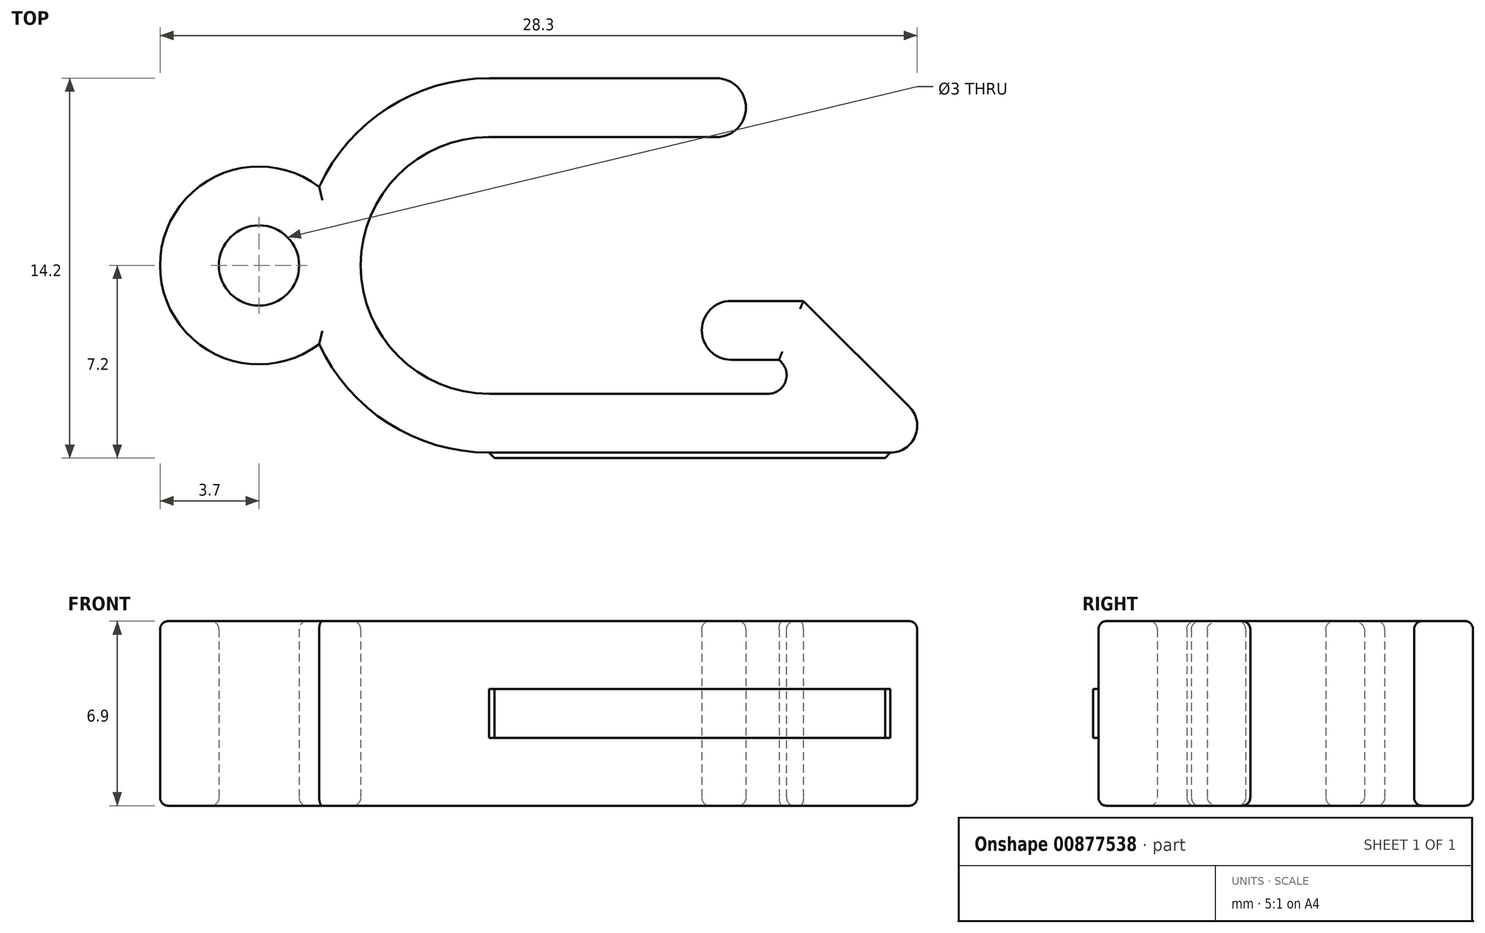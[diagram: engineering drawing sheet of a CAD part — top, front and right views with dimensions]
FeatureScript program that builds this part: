
annotation { "Feature Type Name" : "Feature", "Feature Type Description" : "" }
export const myFeature = defineFeature(function(context is Context, id is Id, definition is map)
    precondition{}
    {
        {
            var Q0;
            Q0=qCreatedBy(makeId("Top.planeOp"),FACE);
            var sketch = newSketch(context, id + "F0", { "sketchPlane" : qUnion([Q0])});
            skArc(sketch, "E0", {"start": v(0, 7) * mm, "mid": v(-7, 0) * mm, "end": v(0, -7) * mm});
            skLineSegment(sketch, "E1", {"start": v(0, 7) * mm, "end": v(8.5, 7) * mm});
            skArc(sketch, "E2", {"start": v(8.5, 7) * mm, "mid": v(9.6, 5.9) * mm, "end": v(8.5, 4.8) * mm});
            skLineSegment(sketch, "E3", {"start": v(8.5, 4.8) * mm, "end": v(0, 4.8) * mm});
            skArc(sketch, "E4", {"start": v(0, 4.8) * mm, "mid": v(-4.8, 0) * mm, "end": v(0, -4.8) * mm});
            skLineSegment(sketch, "E5", {"start": v(0, -4.8) * mm, "end": v(12.11, -4.8) * mm});
            skLineSegment(sketch, "E6", {"start": v(12.11, -4.8) * mm, "end": v(10.84, -3.53) * mm});
            skLineSegment(sketch, "E7", {"start": v(10.84, -3.53) * mm, "end": v(9.05, -3.53) * mm});
            skArc(sketch, "E8", {"start": v(9.05, -3.53) * mm, "mid": v(7.95, -2.43) * mm, "end": v(9.05, -1.33) * mm});
            skLineSegment(sketch, "E9", {"start": v(9.05, -1.33) * mm, "end": v(11.75, -1.33) * mm});
            skLineSegment(sketch, "E10", {"start": v(11.75, -1.33) * mm, "end": v(15.7, -5.29) * mm});
            skLineSegment(sketch, "E11", {"start": v(0, -7) * mm, "end": v(15, -7) * mm});
            skArc(sketch, "E12", {"start": v(15, -7) * mm, "mid": v(15.93, -6.38) * mm, "end": v(15.7, -5.29) * mm});
            skCircle(sketch, "E13", {"center": v(-8.6, 0) * mm, "radius": 1.5 * mm});
            skPoint(sketch, "E13.centerSnap0", {"position": v(-7, 0) * mm});
            skCircle(sketch, "E14", {"center": v(-8.6, 0) * mm, "radius": 3.7 * mm});
            skSolve(sketch);
        }
        {
            var Q0;
            Q0=makeQuery(id+"F0.imprint","IMPRINT",FACE,{"disambiguationData":[TD([[makeQuery(id+"F0.imprint","IMPRINT",EDGE,{"derivedFrom":sQuery(id+"F0.wireOp",EDGE,"E13")}),-1.0]])]});
            var Q1;
            {var subQ0=sQuery(id+"F0.wireOp",EDGE,"E14");var subQ1=sQuery(id+"F0.wireOp",EDGE,"E0");var subQ2=makeQuery(id+"F0.imprint","INTERSECT",VERTEX,{"disambiguationData":[OD(0.0)],"derivedFrom":[subQ1,subQ0]});Q1=makeQuery(id+"F0.imprint","IMPRINT",FACE,{"disambiguationData":[TD([[makeQuery(id+"F0.imprint","IMPRINT",EDGE,{"disambiguationData":[TD([[subQ2,-1.0]])],"derivedFrom":subQ1}),1.0]])]});}
            var Q2;
            {var subQ0=sQuery(id+"F0.wireOp",EDGE,"E1");Q2=makeQuery(id+"F0.imprint","IMPRINT",FACE,{"disambiguationData":[TD([[makeQuery(id+"F0.imprint","IMPRINT",EDGE,{"derivedFrom":subQ0}),-1.0]])]});}
            extrude(context, id + "F1", {"entities" : qUnion([Q0, Q1, Q2]), "depth" : 6.9 * mm, "offsetDistance" : 25 * mm});
        }
        {
            var Q0;
            Q0=makeQuery(id+"F1.opExtrude","SWEPT_EDGE",EDGE,{"disambiguationData":[OSD([sQuery(id+"F0.wireOp",EDGE,"E5"),sQuery(id+"F0.wireOp",EDGE,"E6")])]});
            fillet(context, id + "F2", {"entities" : qUnion([Q0]), "radius" : 0.7 * mm, "tangentPropagation" : true, "allowEdgeOverflow" : false});
        }
        {
            var Q0;
            Q0=makeQuery(id+"F1.opExtrude","CAP_FACE",FACE,{"disambiguationData":[OSD([sQuery(id+"F0.wireOp",EDGE,"E0"),sQuery(id+"F0.wireOp",EDGE,"E1"),sQuery(id+"F0.wireOp",EDGE,"E2"),sQuery(id+"F0.wireOp",EDGE,"E3"),sQuery(id+"F0.wireOp",EDGE,"E4"),sQuery(id+"F0.wireOp",EDGE,"E5"),sQuery(id+"F0.wireOp",EDGE,"E6"),sQuery(id+"F0.wireOp",EDGE,"E7"),sQuery(id+"F0.wireOp",EDGE,"E8"),sQuery(id+"F0.wireOp",EDGE,"E9"),sQuery(id+"F0.wireOp",EDGE,"E10"),sQuery(id+"F0.wireOp",EDGE,"E11"),sQuery(id+"F0.wireOp",EDGE,"E12"),sQuery(id+"F0.wireOp",EDGE,"E13"),sQuery(id+"F0.wireOp",EDGE,"E14")])],"isStart":false});
            var Q1;
            Q1=makeQuery(id+"F1.opExtrude","CAP_FACE",FACE,{"disambiguationData":[OSD([sQuery(id+"F0.wireOp",EDGE,"E0"),sQuery(id+"F0.wireOp",EDGE,"E1"),sQuery(id+"F0.wireOp",EDGE,"E2"),sQuery(id+"F0.wireOp",EDGE,"E3"),sQuery(id+"F0.wireOp",EDGE,"E4"),sQuery(id+"F0.wireOp",EDGE,"E5"),sQuery(id+"F0.wireOp",EDGE,"E6"),sQuery(id+"F0.wireOp",EDGE,"E7"),sQuery(id+"F0.wireOp",EDGE,"E8"),sQuery(id+"F0.wireOp",EDGE,"E9"),sQuery(id+"F0.wireOp",EDGE,"E10"),sQuery(id+"F0.wireOp",EDGE,"E11"),sQuery(id+"F0.wireOp",EDGE,"E12"),sQuery(id+"F0.wireOp",EDGE,"E13"),sQuery(id+"F0.wireOp",EDGE,"E14")])],"isStart":true});
            fillet(context, id + "F3", {"entities" : qUnion([Q0, Q1]), "radius" : 0.3 * mm, "tangentPropagation" : true, "allowEdgeOverflow" : false});
        }
        {
            var Q0;
            Q0=makeQuery(id+"F1.opExtrude","SWEPT_FACE",FACE,{"disambiguationData":[OSD([sQuery(id+"F0.wireOp",EDGE,"E11")])]});
            var sketch = newSketch(context, id + "F4", { "sketchPlane" : qUnion([Q0])});
            skLineSegment(sketch, "E15.bottom", {"start": v(0, 4.37) * mm, "end": v(15, 4.37) * mm});
            skLineSegment(sketch, "E15.top", {"start": v(0, 2.53) * mm, "end": v(15, 2.53) * mm});
            skLineSegment(sketch, "E15.left", {"start": v(0, 4.37) * mm, "end": v(0, 2.53) * mm});
            skLineSegment(sketch, "E15.right", {"start": v(15, 4.37) * mm, "end": v(15, 2.53) * mm});
            skPoint(sketch, "E15.middle", {"position": v(7.5, 3.45) * mm});
            skPoint(sketch, "E15.middle.positionSnap0", {"position": v(0, 3.45) * mm});
            skPoint(sketch, "E15.centerSnap0", {"position": v(0, 3.45) * mm});
            skLineSegment(sketch, "E16", {"start": v(7.5, 6.6) * mm, "end": v(7.5, 0.3) * mm, "construction": true});
            skSolve(sketch);
        }
        {
            var Q0;
            Q0=makeQuery(id+"F4.imprint","IMPRINT",FACE,{"disambiguationData":[TD([[makeQuery(id+"F4.imprint","IMPRINT",EDGE,{"derivedFrom":sQuery(id+"F4.wireOp",EDGE,"E15.bottom")}),-1.0]])]});
            extrude(context, id + "F5", {"entities" : qUnion([Q0]), "operationType" : NewBodyOperationType.ADD, "depth" : 0.2 * mm, "offsetDistance" : 25 * mm});
        }
        {
            var Q0;
            Q0=makeQuery(id+"F5.opExtrude","CAP_EDGE",EDGE,{"disambiguationData":[OSD([sQuery(id+"F4.wireOp",EDGE,"E15.right")])],"isStart":false});
            var Q1;
            Q1=makeQuery(id+"F5.opExtrude","CAP_EDGE",EDGE,{"disambiguationData":[OSD([sQuery(id+"F4.wireOp",EDGE,"E15.left")])],"isStart":false});
            chamfer(context, id + "F6", {"entities" : qUnion([Q0, Q1]), "width" : 0.2 * mm, "tangentPropagation" : true});
        }
    });
